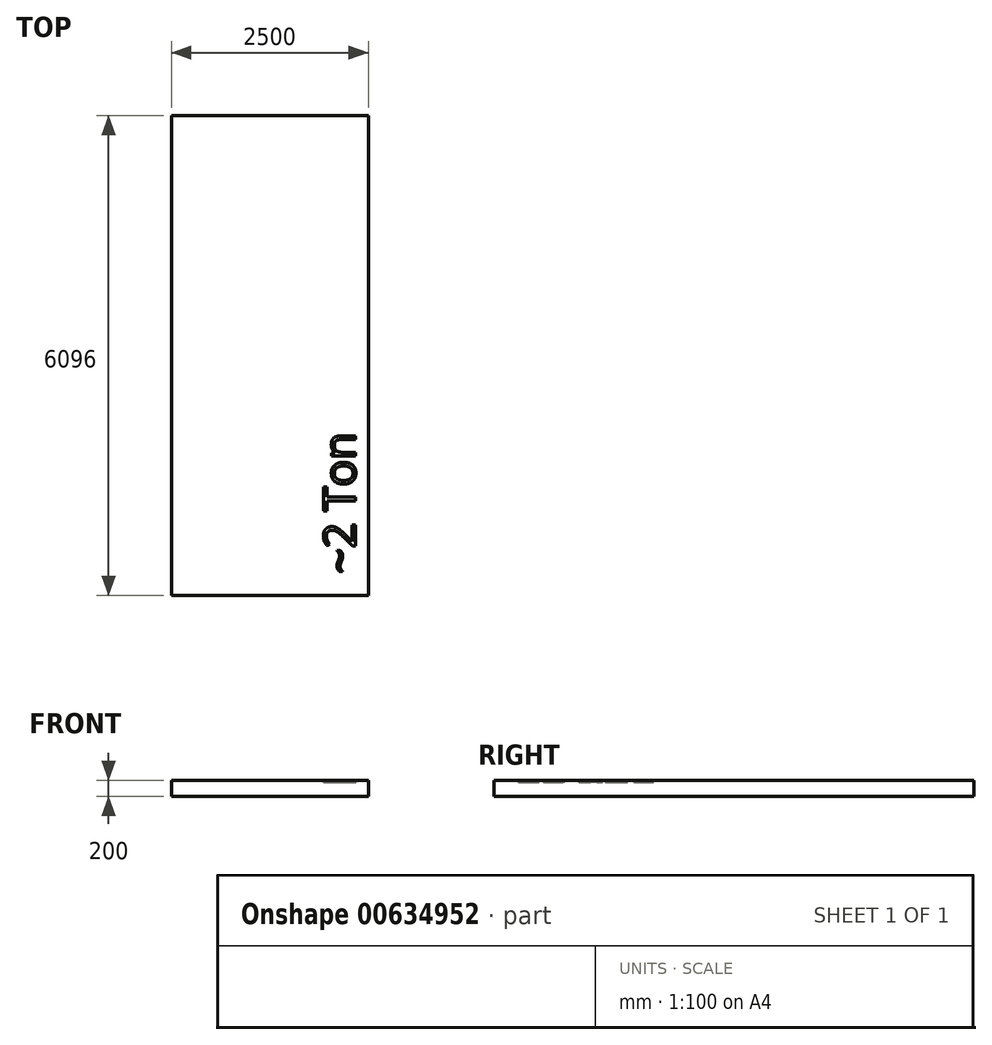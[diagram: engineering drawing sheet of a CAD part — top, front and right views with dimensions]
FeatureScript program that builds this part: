
annotation { "Feature Type Name" : "Feature", "Feature Type Description" : "" }
export const myFeature = defineFeature(function(context is Context, id is Id, definition is map)
    precondition{}
    {
        {
            var Q0;
            Q0=qCreatedBy(makeId("Top.planeOp"),FACE);
            var sketch = newSketch(context, id + "F0", { "sketchPlane" : qUnion([Q0])});
            skLineSegment(sketch, "E0.bottom", {"start": v(-1250, -3048) * mm, "end": v(1250, -3048) * mm});
            skLineSegment(sketch, "E0.top", {"start": v(-1250, 3048) * mm, "end": v(1250, 3048) * mm});
            skLineSegment(sketch, "E0.left", {"start": v(-1250, -3048) * mm, "end": v(-1250, 3048) * mm});
            skLineSegment(sketch, "E0.right", {"start": v(1250, -3048) * mm, "end": v(1250, 3048) * mm});
            skPoint(sketch, "E0.middle", {"position": v(0, 0) * mm});
            skText(sketch, "E1", { "text": "~2 Ton", "fontName": "OpenSans-Regular.ttf"});
            const initialGuessF0  = {"E1": [1.08796, -2.77061, 0, 1, 0.40686]};
            skSetInitialGuess(sketch, initialGuessF0);
            skSolve(sketch);
        }
        {
            var Q0;
            Q0=makeQuery(id+"F0.imprint","IMPRINT",FACE,{"disambiguationData":[TD([[makeQuery(id+"F0.imprint","IMPRINT",EDGE,{"derivedFrom":sQuery(id+"F0.wireOp",EDGE,"E0.bottom")}),1.0]])]});
            var Q1;
            Q1=makeQuery(id+"F0.imprint","IMPRINT",FACE,{"disambiguationData":[TD([[makeQuery(id+"F0.imprint","IMPRINT",EDGE,{"derivedFrom":sQuery(id+"F0.wireOp",EDGE,"E1.sketch_text.stroke-0")}),-1.0]])]});
            var Q2;
            Q2=makeQuery(id+"F0.imprint","IMPRINT",FACE,{"disambiguationData":[TD([[makeQuery(id+"F0.imprint","IMPRINT",EDGE,{"derivedFrom":sQuery(id+"F0.wireOp",EDGE,"E1.sketch_text.stroke-16")}),-1.0]])]});
            var Q3;
            Q3=makeQuery(id+"F0.imprint","IMPRINT",FACE,{"disambiguationData":[TD([[makeQuery(id+"F0.imprint","IMPRINT",EDGE,{"derivedFrom":sQuery(id+"F0.wireOp",EDGE,"E1.sketch_text.stroke-36")}),-1.0]])]});
            var Q4;
            Q4=makeQuery(id+"F0.imprint","IMPRINT",FACE,{"disambiguationData":[TD([[makeQuery(id+"F0.imprint","IMPRINT",EDGE,{"derivedFrom":sQuery(id+"F0.wireOp",EDGE,"E1.sketch_text.stroke-44")}),-1.0]])]});
            var Q5;
            Q5=makeQuery(id+"F0.imprint","IMPRINT",FACE,{"disambiguationData":[TD([[makeQuery(id+"F0.imprint","IMPRINT",EDGE,{"derivedFrom":sQuery(id+"F0.wireOp",EDGE,"E1.sketch_text.stroke-53")}),1.0]])]});
            var Q6;
            Q6=makeQuery(id+"F0.imprint","IMPRINT",FACE,{"disambiguationData":[TD([[makeQuery(id+"F0.imprint","IMPRINT",EDGE,{"derivedFrom":sQuery(id+"F0.wireOp",EDGE,"E1.sketch_text.stroke-61")}),-1.0]])]});
            extrude(context, id + "F1", {"entities" : qUnion([Q0, Q1, Q2, Q3, Q4, Q5, Q6]), "oppositeDirection" : true, "depth" : 200 * mm, "offsetDistance" : 25 * mm});
        }
        {
            var Q0;
            Q0=makeQuery(id+"F0.imprint","IMPRINT",FACE,{"disambiguationData":[TD([[makeQuery(id+"F0.imprint","IMPRINT",EDGE,{"derivedFrom":sQuery(id+"F0.wireOp",EDGE,"E1.sketch_text.stroke-16")}),-1.0]])]});
            var Q1;
            Q1=makeQuery(id+"F0.imprint","IMPRINT",FACE,{"disambiguationData":[TD([[makeQuery(id+"F0.imprint","IMPRINT",EDGE,{"derivedFrom":sQuery(id+"F0.wireOp",EDGE,"E1.sketch_text.stroke-0")}),-1.0]])]});
            var Q2;
            Q2=makeQuery(id+"F0.imprint","IMPRINT",FACE,{"disambiguationData":[TD([[makeQuery(id+"F0.imprint","IMPRINT",EDGE,{"derivedFrom":sQuery(id+"F0.wireOp",EDGE,"E1.sketch_text.stroke-36")}),-1.0]])]});
            var Q3;
            Q3=makeQuery(id+"F0.imprint","IMPRINT",FACE,{"disambiguationData":[TD([[makeQuery(id+"F0.imprint","IMPRINT",EDGE,{"derivedFrom":sQuery(id+"F0.wireOp",EDGE,"E1.sketch_text.stroke-44")}),-1.0]])]});
            var Q4;
            Q4=makeQuery(id+"F0.imprint","IMPRINT",FACE,{"disambiguationData":[TD([[makeQuery(id+"F0.imprint","IMPRINT",EDGE,{"derivedFrom":sQuery(id+"F0.wireOp",EDGE,"E1.sketch_text.stroke-61")}),-1.0]])]});
            extrude(context, id + "F2", {"entities" : qUnion([Q0, Q1, Q2, Q3, Q4]), "operationType" : NewBodyOperationType.REMOVE, "oppositeDirection" : true, "depth" : 25 * mm, "offsetDistance" : 25 * mm});
        }
    });
